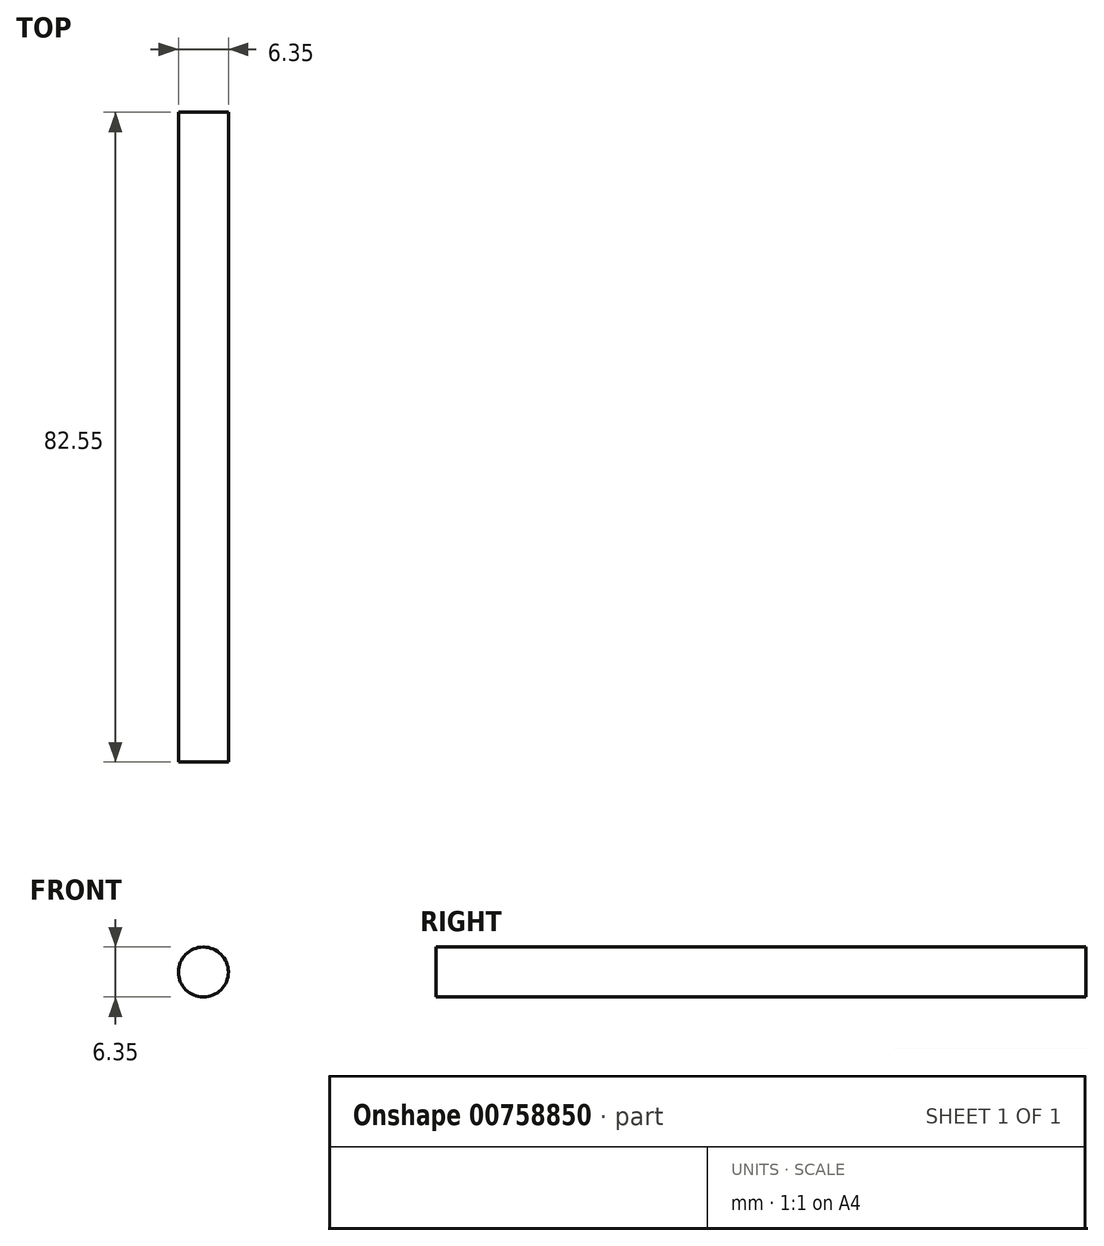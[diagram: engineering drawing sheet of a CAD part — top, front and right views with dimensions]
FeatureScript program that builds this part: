
annotation { "Feature Type Name" : "Feature", "Feature Type Description" : "" }
export const myFeature = defineFeature(function(context is Context, id is Id, definition is map)
    precondition{}
    {
        {
            var Q0;
            Q0=qCreatedBy(makeId("Front.planeOp"),FACE);
            var sketch = newSketch(context, id + "F0", { "sketchPlane" : qUnion([Q0])});
            skCircle(sketch, "E0", {"center": v(-33.2, 23.44) * mm, "radius": 3.18 * mm});
            skSolve(sketch);
        }
        {
            var Q0;
            Q0 = qSketchRegion(id + "F0", true);
            extrude(context, id + "F1", {"entities" : qUnion([Q0]), "depth" : 82.55 * mm, "offsetDistance" : 25.4 * mm});
        }
    });
